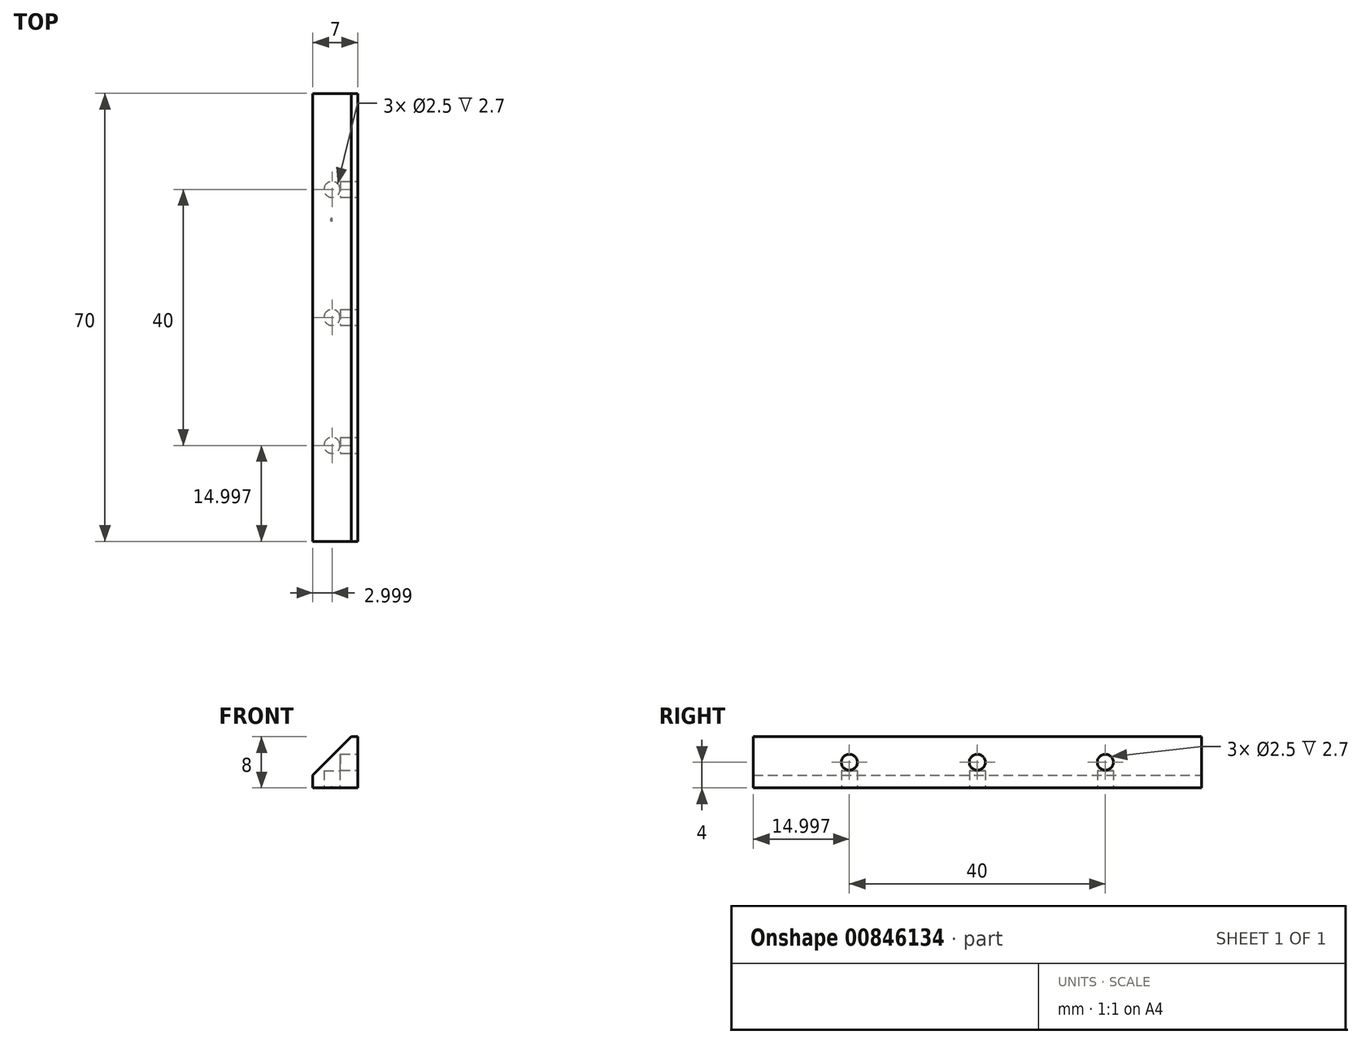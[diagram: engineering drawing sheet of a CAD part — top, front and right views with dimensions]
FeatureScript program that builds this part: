
annotation { "Feature Type Name" : "Feature", "Feature Type Description" : "" }
export const myFeature = defineFeature(function(context is Context, id is Id, definition is map)
    precondition{}
    {
        {
            var Q0;
            Q0=qCreatedBy(makeId("Top.planeOp"),FACE);
            var sketch = newSketch(context, id + "F0", { "sketchPlane" : qUnion([Q0])});
            skLineSegment(sketch, "E0.bottom", {"start": v(-14.75, 31.83) * mm, "end": v(-7.75, 31.83) * mm});
            skLineSegment(sketch, "E0.top", {"start": v(-14.75, -38.17) * mm, "end": v(-7.75, -38.17) * mm});
            skLineSegment(sketch, "E0.left", {"start": v(-14.75, 31.83) * mm, "end": v(-14.75, -38.17) * mm});
            skLineSegment(sketch, "E0.right", {"start": v(-7.75, 31.83) * mm, "end": v(-7.75, -38.17) * mm});
            skSolve(sketch);
        }
        {
            var Q0;
            Q0 = qSketchRegion(id + "F0", true);
            extrude(context, id + "F1", {"entities" : qUnion([Q0]), "depth" : 8 * mm, "offsetDistance" : 25 * mm});
        }
        {
            var Q0;
            Q0=makeQuery(id+"F1.opExtrude","CAP_EDGE",EDGE,{"disambiguationData":[OSD([sQuery(id+"F0.wireOp",EDGE,"E0.left")])],"isStart":false});
            chamfer(context, id + "F2", {"entities" : qUnion([Q0]), "width" : 6 * mm, "tangentPropagation" : true});
        }
        {
            var Q0;
            Q0=makeQuery(id+"F1.opExtrude","SWEPT_FACE",FACE,{"disambiguationData":[OSD([sQuery(id+"F0.wireOp",EDGE,"E0.right")])]});
            var sketch = newSketch(context, id + "F3", { "sketchPlane" : qUnion([Q0])});
            skLineSegment(sketch, "E1", {"start": v(-38.17, 0) * mm, "end": v(-23.17, 0) * mm});
            skLineSegment(sketch, "E2", {"start": v(-23.17, 0) * mm, "end": v(-23.17, 4) * mm});
            skLineSegment(sketch, "E3", {"start": v(31.83, 0) * mm, "end": v(16.83, 0) * mm});
            skLineSegment(sketch, "E4", {"start": v(16.83, 0) * mm, "end": v(16.83, 4) * mm});
            skLineSegment(sketch, "E5", {"start": v(16.83, 0) * mm, "end": v(-3.17, 0) * mm});
            skCircle(sketch, "E6", {"center": v(-23.17, 4) * mm, "radius": 1.25 * mm});
            skCircle(sketch, "E7", {"center": v(-3.17, 4) * mm, "radius": 1.25 * mm});
            skCircle(sketch, "E8", {"center": v(16.83, 4) * mm, "radius": 1.25 * mm});
            skSolve(sketch);
        }
        {
            var Q0;
            Q0 = qSketchRegion(id + "F3", true);
            extrude(context, id + "F4", {"entities" : qUnion([Q0]), "operationType" : NewBodyOperationType.REMOVE, "oppositeDirection" : true, "depth" : 2.7 * mm, "offsetDistance" : 25 * mm});
        }
        {
            var Q0;
            Q0=makeQuery(id+"F1.opExtrude","CAP_FACE",FACE,{"disambiguationData":[OSD([sQuery(id+"F0.wireOp",EDGE,"E0.bottom"),sQuery(id+"F0.wireOp",EDGE,"E0.top"),sQuery(id+"F0.wireOp",EDGE,"E0.left"),sQuery(id+"F0.wireOp",EDGE,"E0.right")])],"isStart":true});
            var sketch = newSketch(context, id + "F5", { "sketchPlane" : qUnion([Q0])});
            skLineSegment(sketch, "E9", {"start": v(-7.75, -31.83) * mm, "end": v(-7.75, -16.83) * mm});
            skLineSegment(sketch, "E10", {"start": v(-7.75, -16.83) * mm, "end": v(-11.75, -16.83) * mm});
            skLineSegment(sketch, "E11", {"start": v(-7.75, 38.17) * mm, "end": v(-7.75, 23.17) * mm});
            skLineSegment(sketch, "E12", {"start": v(-7.75, 23.17) * mm, "end": v(-11.75, 23.17) * mm});
            skLineSegment(sketch, "E13", {"start": v(-7.75, 23.17) * mm, "end": v(-7.75, 3.17) * mm});
            skLineSegment(sketch, "E14", {"start": v(-7.75, 3.17) * mm, "end": v(-11.75, 3.17) * mm});
            skCircle(sketch, "E15", {"center": v(-11.75, -16.83) * mm, "radius": 1.25 * mm});
            skCircle(sketch, "E16", {"center": v(-11.75, 3.17) * mm, "radius": 1.25 * mm});
            skCircle(sketch, "E17", {"center": v(-11.75, 23.17) * mm, "radius": 1.25 * mm});
            skLineSegment(sketch, "E18", {"start": v(-11.75, -16.83) * mm, "end": v(-11.75, -11.83) * mm, "construction": true});
            skLineSegment(sketch, "E19.bottom", {"start": v(-11.75, -11.83) * mm, "end": v(-11.95, -11.83) * mm});
            skLineSegment(sketch, "E19.top", {"start": v(-11.75, -12.33) * mm, "end": v(-11.95, -12.33) * mm});
            skLineSegment(sketch, "E19.left", {"start": v(-11.75, -11.83) * mm, "end": v(-11.75, -12.33) * mm});
            skLineSegment(sketch, "E19.right", {"start": v(-11.95, -11.83) * mm, "end": v(-11.95, -12.33) * mm});
            skSolve(sketch);
        }
        {
            var Q0;
            Q0=makeQuery(id+"F5.imprint","IMPRINT",FACE,{"disambiguationData":[TD([[makeQuery(id+"F5.imprint","IMPRINT",EDGE,{"derivedFrom":sQuery(id+"F5.wireOp",EDGE,"E15")}),1.0]])]});
            var Q1;
            Q1=makeQuery(id+"F5.imprint","IMPRINT",FACE,{"disambiguationData":[TD([[makeQuery(id+"F5.imprint","IMPRINT",EDGE,{"derivedFrom":sQuery(id+"F5.wireOp",EDGE,"E16")}),1.0]])]});
            var Q2;
            Q2=makeQuery(id+"F5.imprint","IMPRINT",FACE,{"disambiguationData":[TD([[makeQuery(id+"F5.imprint","IMPRINT",EDGE,{"derivedFrom":sQuery(id+"F5.wireOp",EDGE,"E17")}),1.0]])]});
            extrude(context, id + "F6", {"entities" : qUnion([Q0, Q1, Q2]), "operationType" : NewBodyOperationType.REMOVE, "oppositeDirection" : true, "depth" : 2.7 * mm, "offsetDistance" : 25 * mm});
        }
        {
            var Q0;
            Q0=makeQuery(id+"F5.imprint","IMPRINT",FACE,{"disambiguationData":[TD([[makeQuery(id+"F5.imprint","IMPRINT",EDGE,{"derivedFrom":sQuery(id+"F5.wireOp",EDGE,"E19.bottom")}),1.0]])]});
            extrude(context, id + "F7", {"entities" : qUnion([Q0]), "operationType" : NewBodyOperationType.REMOVE, "oppositeDirection" : true, "depth" : 0.15 * mm, "offsetDistance" : 25 * mm});
        }
    });
